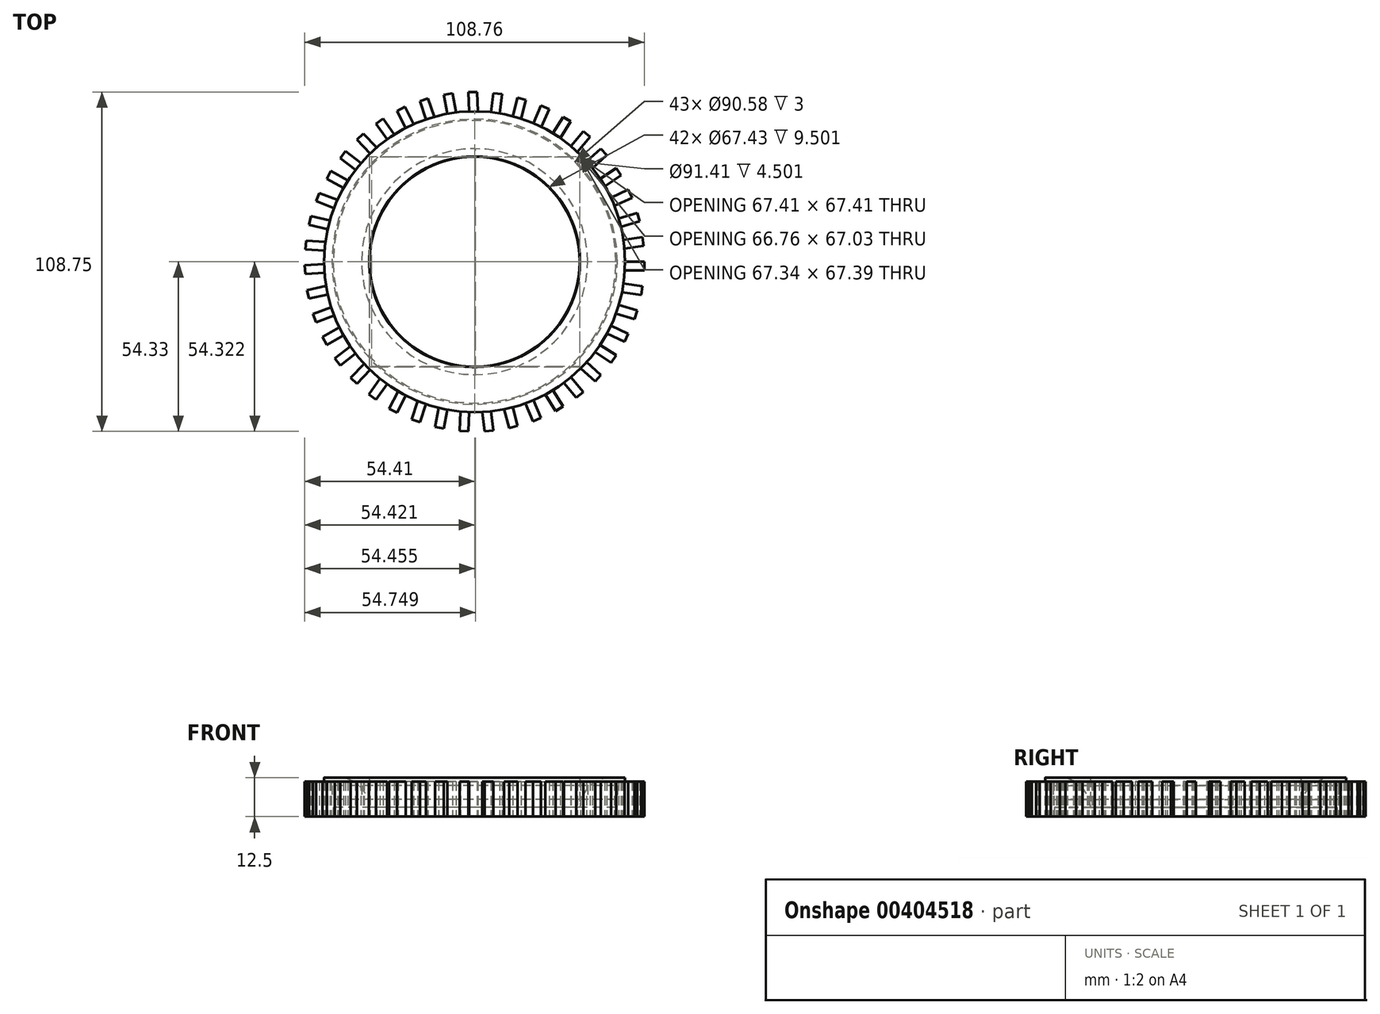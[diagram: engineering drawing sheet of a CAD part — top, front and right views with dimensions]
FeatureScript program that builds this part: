
annotation { "Feature Type Name" : "Feature", "Feature Type Description" : "" }
export const myFeature = defineFeature(function(context is Context, id is Id, definition is map)
    precondition{}
    {
        {
            var Q0;
            Q0=qCreatedBy(makeId("Top.planeOp"),FACE);
            var sketch = newSketch(context, id + "F0", { "sketchPlane" : qUnion([Q0])});
            skCircle(sketch, "E0", {"center": v(0, 0) * mm, "radius": 48.2 * mm});
            skSolve(sketch);
        }
        {
            var Q0;
            Q0=makeQuery(id+"F0.imprint","IMPRINT",FACE,{"disambiguationData":[TD([[makeQuery(id+"F0.imprint","IMPRINT",EDGE,{"derivedFrom":sQuery(id+"F0.wireOp",EDGE,"E0")}),1.0]])]});
            extrude(context, id + "F1", {"entities" : qUnion([Q0]), "depth" : 12.5 * mm});
        }
        {
            var Q0;
            Q0=qCreatedBy(makeId("Top.planeOp"),FACE);
            var sketch = newSketch(context, id + "F2", { "sketchPlane" : qUnion([Q0])});
            skCircle(sketch, "E1", {"center": v(0, 0) * mm, "radius": 33.72 * mm});
            skSolve(sketch);
        }
        {
            var Q0;
            Q0 = qSketchRegion(id + "F2", true);
            extrude(context, id + "F3", {"entities" : qUnion([Q0]), "operationType" : NewBodyOperationType.REMOVE, "depth" : 55.72 * mm});
        }
        {
            var Q0;
            Q0=qCreatedBy(makeId("Top.planeOp"),FACE);
            var sketch = newSketch(context, id + "F4", { "sketchPlane" : qUnion([Q0])});
            skLineSegment(sketch, "E2.bottom", {"start": v(48.1, 0) * mm, "end": v(54.35, 0) * mm});
            skLineSegment(sketch, "E2.top", {"start": v(48.1, -2.81) * mm, "end": v(54.35, -2.81) * mm});
            skLineSegment(sketch, "E2.left", {"start": v(48.1, 0) * mm, "end": v(48.1, -2.81) * mm});
            skLineSegment(sketch, "E2.right", {"start": v(54.35, 0) * mm, "end": v(54.35, -2.81) * mm});
            skSolve(sketch);
        }
        {
            var Q0;
            Q0=makeQuery(id+"F4.imprint","IMPRINT",FACE,{"disambiguationData":[TD([[makeQuery(id+"F4.imprint","IMPRINT",EDGE,{"derivedFrom":sQuery(id+"F4.wireOp",EDGE,"E2.bottom")}),-1.0]])]});
            extrude(context, id + "F5", {"entities" : qUnion([Q0]), "operationType" : NewBodyOperationType.ADD, "depth" : 11.25 * mm});
        }
        {
            var Q0;
            Q0=qCreatedBy(makeId("Front.planeOp"),FACE);
            var sketch = newSketch(context, id + "F6", { "sketchPlane" : qUnion([Q0])});
            skLineSegment(sketch, "E3", {"start": v(0, -67.8) * mm, "end": v(0, 82.29) * mm});
            skSolve(sketch);
        }
        {
            var Q0;
            Q0=makeQuery(id+"F1.opExtrude","SWEPT_BODY",BODY,{"disambiguationData":[OSD([sQuery(id+"F0.wireOp",EDGE,"E0")])]});
            var Q1;
            Q1=sQuery(id+"F6.wireOp",EDGE,"E3");
            circularPattern(context, id + "F7", {"entities" : qUnion([Q0]), "axis" : qUnion([Q1]), "angle" : 360 * degree, "instanceCount" : 43, "oppositeDirection" : true, "equalSpace" : true});
        }
        {
            var Q0;
            Q0=qCreatedBy(makeId("Top.planeOp"),FACE);
            var sketch = newSketch(context, id + "F8", { "sketchPlane" : qUnion([Q0])});
            skCircle(sketch, "E4", {"center": v(0, 0) * mm, "radius": 45.3 * mm});
            skSolve(sketch);
        }
        {
            var Q0;
            Q0=qCreatedBy(makeId("Top.planeOp"),FACE);
            var sketch = newSketch(context, id + "F9", { "sketchPlane" : qUnion([Q0])});
            skCircle(sketch, "E5", {"center": v(0, 0) * mm, "radius": 41.76 * mm});
            skSolve(sketch);
        }
        {
            var Q0;
            Q0=makeQuery(id+"F8.imprint","IMPRINT",FACE,{"disambiguationData":[TD([[makeQuery(id+"F8.imprint","IMPRINT",EDGE,{"derivedFrom":sQuery(id+"F8.wireOp",EDGE,"E4")}),1.0]])]});
            var Q1;
            Q1 = qSketchRegion(id + "F9", true);
            extrude(context, id + "F10", {"entities" : qUnion([Q0, Q1]), "operationType" : NewBodyOperationType.REMOVE, "depth" : 3 * mm});
        }
        {
            var Q0;
            Q0=makeQuery(id+"F7.opPattern","COPY",FACE,{"derivedFrom":makeQuery(id+"F1.opExtrude","CAP_FACE",FACE,{"disambiguationData":[OSD([sQuery(id+"F0.wireOp",EDGE,"E0")])],"isStart":false}),"instanceName":"36"});
            var Q1;
            Q1=makeQuery(id+"F7.opPattern","COPY",BODY,{"derivedFrom":makeQuery(id+"F1.opExtrude","SWEPT_BODY",BODY,{"disambiguationData":[OSD([sQuery(id+"F0.wireOp",EDGE,"E0")])]}),"instanceName":"23"});
            shell(context, id + "F11", {"isHollow" : true, "entities" : qUnion([Q0]), "parts" : qUnion([Q1]), "thickness" : 2.5 * mm});
        }
        {
            var Q0;
            Q0=makeQuery(id+"F7.opPattern","COPY",EDGE,{"derivedFrom":makeQuery(id+"F3.boolean.opBoolean","INTERSECT",EDGE,{"derivedFrom":[makeQuery(id+"F1.opExtrude","CAP_FACE",FACE,{"disambiguationData":[OSD([sQuery(id+"F0.wireOp",EDGE,"E0")])],"isStart":false}),makeQuery(id+"F3.opExtrude","SWEPT_FACE",FACE,{"disambiguationData":[OSD([sQuery(id+"F2.wireOp",EDGE,"E1")])]})]}),"instanceName":"40"});
            fillet(context, id + "F12", {"entities" : qUnion([Q0]), "radius" : 10 * mm, "tangentPropagation" : true, "allowEdgeOverflow" : false});
        }
    });
